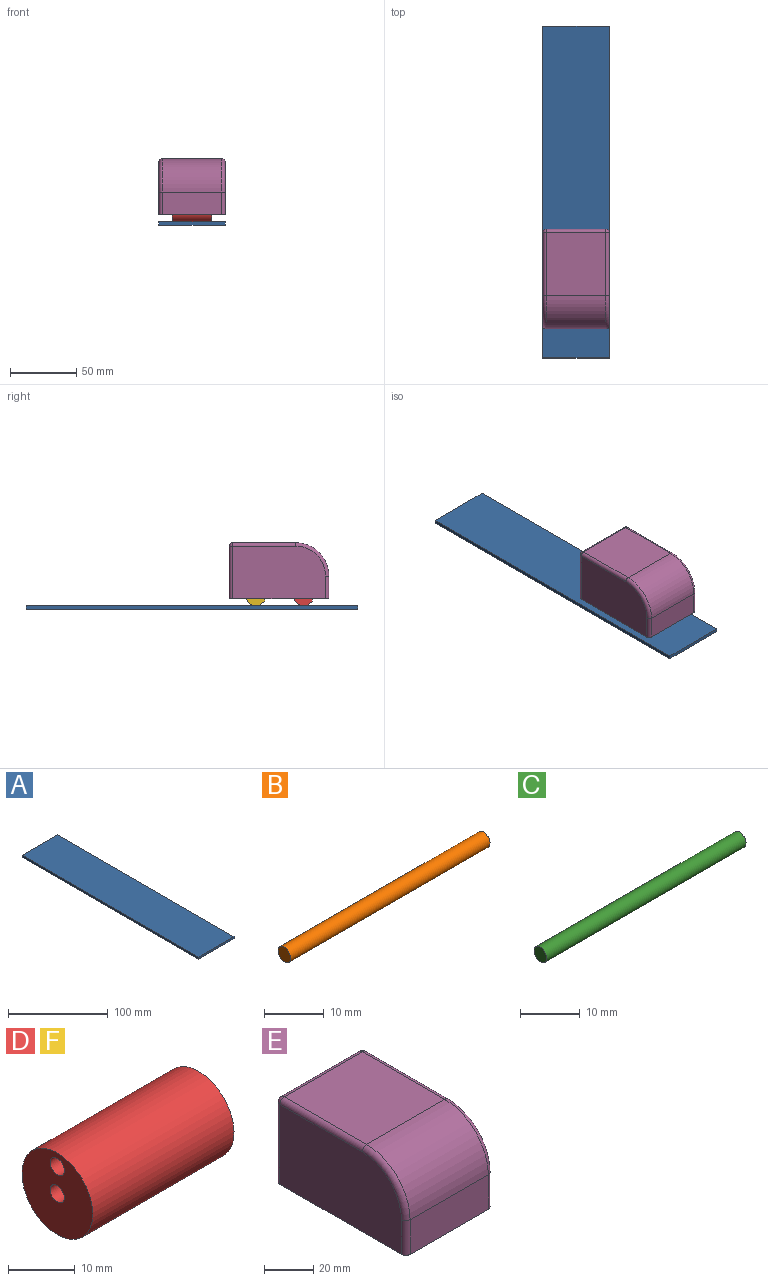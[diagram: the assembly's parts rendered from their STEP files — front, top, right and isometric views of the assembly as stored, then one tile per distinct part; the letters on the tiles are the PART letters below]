
ASSEMBLY  parts=6 mates=5
PART A: 6 faces, bbox 50x250x2.5 mm
  f0: plane 50x2.5mm, normal (0,1,0), area 125mm2, adj f1,f3,f4,f5
  f1: plane 250x2.5mm, normal (-1,0,0), area 625mm2, adj f0,f2,f4,f5
  f2: plane 50x2.5mm, normal (0,-1,0), area 125mm2, adj f1,f3,f4,f5
  f3: plane 250x2.5mm, normal (1,0,0), area 625mm2, adj f0,f2,f4,f5
  f4: plane 250x50mm, normal (0,0,-1), area 12500mm2, adj f0,f1,f2,f3
  f5: plane 250x50mm, normal (0,0,1), area 12500mm2, adj f0,f1,f2,f3
PART B: 3 faces, bbox 47x3x3 mm
  f0: cylinder r=1.5mm len=47mm, axis (-1,0,0), area 443mm2, adj f1,f2
  f1: plane 3x3mm, normal (1,0,0), area 7.1mm2, adj f0
  f2: plane 3x3mm, normal (-1,0,0), area 7.1mm2, adj f0
PART C: 3 faces, bbox 47x3x3 mm
  f0: cylinder r=1.5mm len=47mm, axis (-1,0,0), area 443mm2, adj f1,f2
  f1: plane 3x3mm, normal (1,0,0), area 7.1mm2, adj f0
  f2: plane 3x3mm, normal (-1,0,0), area 7.1mm2, adj f0
PART D: 5 faces, bbox 30x15x15 mm
  f0: cylinder r=1.5mm len=30mm, axis (-1,0,0), area 282.7mm2, adj f2,f3
  f1: cylinder r=7.5mm len=30mm, axis (-1,0,0), area 1413.7mm2, adj f2,f3
  f2: plane 15x15mm, normal (1,0,0), area 162.6mm2, adj f0,f1,f4
  f3: plane 15x15mm, normal (-1,0,0), area 162.6mm2, adj f0,f1,f4
  f4: cylinder r=1.5mm len=30mm, axis (-1,0,0), area 282.7mm2, adj f2,f3
PART E: 32 faces, bbox 50x77.1x44.4 mm
  f0: cylinder r=25mm len=45mm, axis (-1,0,0), area 1767.1mm2, adj f1,f4,f22,f30
  f1: plane 45x17.3mm, normal (0,-1,0), area 778.5mm2, adj f0,f6,f21,f31
  f2: plane 70x39.8mm, normal (1,0,0), area 2677.4mm2, adj f6,f21,f22,f23,f24
  f3: plane 70x39.8mm, normal (-1,0,0), area 2677.4mm2, adj f6,f26,f29,f30,f31
  f4: plane 47.5x45mm, normal (0,0,1), area 2137.5mm2, adj f0,f24,f27,f29
  f5: plane 45x39.8mm, normal (0,1,0), area 1791mm2, adj f6,f23,f26,f27
  f6: plane 75x50mm, normal (0,0,-1), area 1144.6mm2, adj f1,f2,f3,f5,f9,f10,f11,f12
  f7: plane 45x40mm, normal (0,0,-1), area 1800mm2, adj f8,f9,f11,f12
  f8: cylinder r=20mm len=40mm, axis (-1,0,0), area 1256.6mm2, adj f7,f9,f10,f11
  f9: plane 65x37.3mm, normal (-1,0,0), area 2324.5mm2, adj f6,f7,f8,f10,f12,f17,f19
  f10: plane 40x17.3mm, normal (0,1,0), area 692mm2, adj f6,f8,f9,f11
  f11: plane 65x37.3mm, normal (1,0,0), area 2324.5mm2, adj f6,f7,f8,f10,f12,f14,f16
  f12: plane 40x37.3mm, normal (0,-1,0), area 1492mm2, adj f6,f7,f9,f11
  f13: plane 3x3mm, normal (1,0,0), area 7.1mm2, adj f14
  f14: cylinder r=1.5mm len=3.5mm, axis (-1,0,0), area 33mm2, adj f11,f13
  f15: plane 3x3mm, normal (1,0,0), area 7.1mm2, adj f16
  f16: cylinder r=1.5mm len=3.5mm, axis (-1,0,0), area 33mm2, adj f11,f15
  f17: cylinder r=1.5mm len=3.5mm, axis (-1,0,0), area 33mm2, adj f9,f18
  f18: plane 3x3mm, normal (-1,0,0), area 7.1mm2, adj f17
  f19: cylinder r=1.5mm len=3.5mm, axis (-1,0,0), area 33mm2, adj f9,f20
  f20: plane 3x3mm, normal (-1,0,0), area 7.1mm2, adj f19
  f21: cylinder r=2.5mm len=17.3mm, axis (0,0,1), area 67.9mm2, adj f1,f2,f6,f22
  f22: torus R=22.5mm, axis (1,0,0), area 148.6mm2, adj f0,f2,f21,f24
  f23: cylinder r=2.5mm len=39.8mm, axis (0,0,-1), area 156.3mm2, adj f2,f5,f6,f25
  f24: cylinder r=2.5mm len=47.5mm, axis (0,-1,0), area 186.5mm2, adj f2,f4,f22,f25
  f25: sphere r=2.5mm, area 9.8mm2, adj f23,f24,f27
  f26: cylinder r=2.5mm len=39.8mm, axis (0,0,1), area 156.3mm2, adj f3,f5,f6,f28
  f27: cylinder r=2.5mm len=45mm, axis (1,0,0), area 176.7mm2, adj f4,f5,f25,f28
  f28: sphere r=2.5mm, area 9.8mm2, adj f26,f27,f29
  f29: cylinder r=2.5mm len=47.5mm, axis (0,1,0), area 186.5mm2, adj f3,f4,f28,f30
  f30: torus R=22.5mm, axis (1,0,0), area 148.6mm2, adj f0,f3,f29,f31
  f31: cylinder r=2.5mm len=17.3mm, axis (0,0,-1), area 67.9mm2, adj f1,f3,f6,f30
PART F: same geometry as D
PLACE A at identity fixed
PLACE B t=(0,-78.07,7.5)mm
PLACE C t=(0,-78.07,7.5)mm
PLACE D rot(axis=(1,0,0),89.4deg) t=(0,-84,13.5)mm
PLACE E t=(0,-78.07,7.5)mm
PLACE F rot(axis=(1,0,0),89.4deg) t=(0,-48,13.5)mm
MATE fastened E.f14 <-> C.f0  axis (1,0,0) through (-23.5,-48.07,7.5)mm
MATE slider A.f0 <-> E.f5  axis (0,1,0) through (0,125,0)mm
MATE revolute D.f1 <-> E.f16  axis (-1,0,0) through (0,-84.07,7.5)mm
MATE revolute F.f1 <-> C.f0  axis (-1,0,0) through (0,-48.07,7.5)mm
MATE fastened B.f0 <-> E.f16  axis (-1,0,0) through (0,-84.07,7.5)mm
